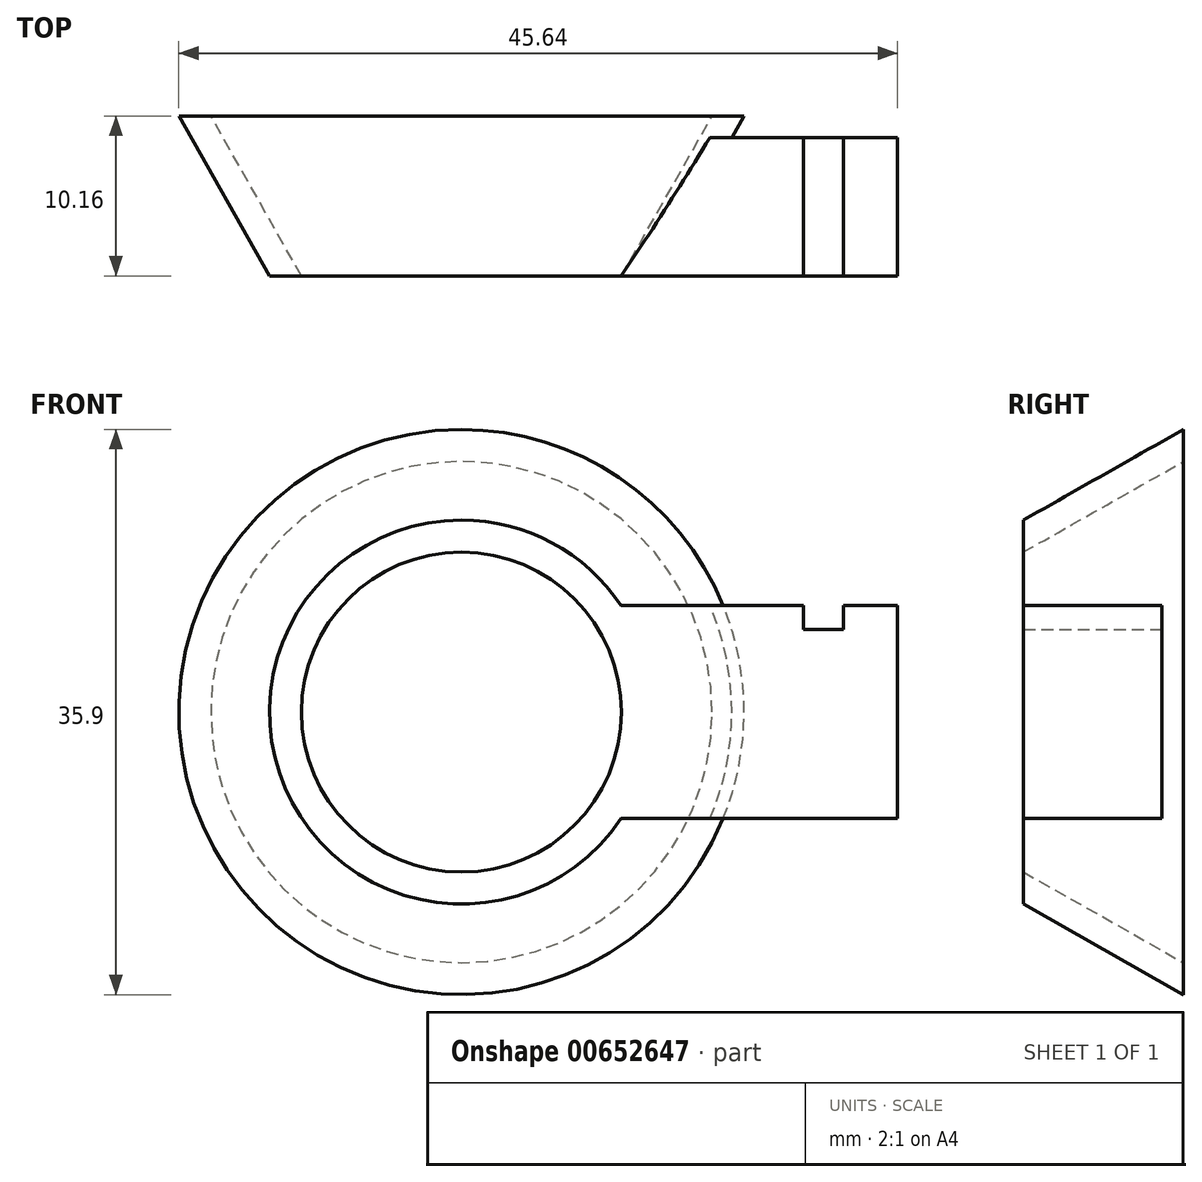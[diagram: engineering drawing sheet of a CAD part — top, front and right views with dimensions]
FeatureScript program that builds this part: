
annotation { "Feature Type Name" : "Feature", "Feature Type Description" : "" }
export const myFeature = defineFeature(function(context is Context, id is Id, definition is map)
    precondition{}
    {
        {
            var Q0;
            Q0=qCreatedBy(makeId("Top.planeOp"),FACE);
            var sketch = newSketch(context, id + "F0", { "sketchPlane" : qUnion([Q0])});
            skLineSegment(sketch, "E0.bottom", {"start": v(-10.16, -10.16) * mm, "end": v(10.16, -10.16) * mm, "construction": true});
            skLineSegment(sketch, "E0.top", {"start": v(-10.16, 10.16) * mm, "end": v(10.16, 10.16) * mm, "construction": true});
            skLineSegment(sketch, "E0.left", {"start": v(-10.16, -10.16) * mm, "end": v(-10.16, 10.16) * mm, "construction": true});
            skLineSegment(sketch, "E0.right", {"start": v(10.16, -10.16) * mm, "end": v(10.16, 10.16) * mm, "construction": true});
            skPoint(sketch, "E0.middle", {"position": v(0, 0) * mm});
            skLineSegment(sketch, "E1", {"start": v(-10.16, 0) * mm, "end": v(-15.92, 10.16) * mm});
            skLineSegment(sketch, "E2", {"start": v(-15.92, 10.16) * mm, "end": v(-17.95, 10.16) * mm});
            skLineSegment(sketch, "E3", {"start": v(-17.95, 10.16) * mm, "end": v(-12.2, 0) * mm});
            skLineSegment(sketch, "E4", {"start": v(-12.2, 0) * mm, "end": v(-10.16, 0) * mm});
            skLineSegment(sketch, "E5", {"start": v(0, 14.27) * mm, "end": v(0, -5.58) * mm});
            skSolve(sketch);
        }
        {
            var Q0;
            Q0=makeQuery(id+"F0.imprint","IMPRINT",FACE,{"disambiguationData":[TD([[makeQuery(id+"F0.imprint","IMPRINT",EDGE,{"derivedFrom":sQuery(id+"F0.wireOp",EDGE,"E1")}),1.0]])]});
            var Q1;
            Q1=sQuery(id+"F0.wireOp",EDGE,"E5");
            revolve(context, id + "F1", {"entities" : qUnion([Q0]), "axis" : qUnion([Q1]), "revolveType" : RevolveType.FULL});
        }
        {
            var Q0;
            Q0=qCreatedBy(makeId("Right.planeOp"),FACE);
            cPlane(context, id + "F2", {"entities" : qUnion([Q0]), "cplaneType" : CPlaneType.OFFSET, "offset" : 17.53 * mm, "width" : 152.4 * mm, "height" : 152.4 * mm});
        }
        {
            var Q0;
            Q0=qCreatedBy(id+"F2.planeOp",FACE);
            var sketch = newSketch(context, id + "F3", { "sketchPlane" : qUnion([Q0])});
            skLineSegment(sketch, "E6.bottom", {"start": v(0, 6.76) * mm, "end": v(8.79, 6.76) * mm});
            skLineSegment(sketch, "E6.top", {"start": v(0, -6.76) * mm, "end": v(8.79, -6.76) * mm});
            skLineSegment(sketch, "E6.left", {"start": v(0, 6.76) * mm, "end": v(0, -6.76) * mm});
            skLineSegment(sketch, "E6.right", {"start": v(8.79, 6.76) * mm, "end": v(8.79, -6.76) * mm});
            skPoint(sketch, "E6.middle", {"position": v(4.4, 0) * mm});
            skSolve(sketch);
        }
        {
            var Q0;
            Q0=makeQuery(id+"F3.imprint","IMPRINT",FACE,{"disambiguationData":[TD([[makeQuery(id+"F3.imprint","IMPRINT",EDGE,{"derivedFrom":sQuery(id+"F3.wireOp",EDGE,"E6.bottom")}),-1.0]])]});
            extrude(context, id + "F4", {"entities" : qUnion([Q0]), "operationType" : NewBodyOperationType.ADD, "endBound" : BoundingType.UP_TO_NEXT, "oppositeDirection" : true, "depth" : 25.4 * mm, "offsetDistance" : 25.4 * mm});
        }
        {
            var Q0;
            Q0=makeQuery(id+"F4.opExtrude","CAP_FACE",FACE,{"disambiguationData":[OSD([sQuery(id+"F3.wireOp",EDGE,"E6.bottom"),sQuery(id+"F3.wireOp",EDGE,"E6.top"),sQuery(id+"F3.wireOp",EDGE,"E6.left"),sQuery(id+"F3.wireOp",EDGE,"E6.right")])],"isStart":true});
            extrude(context, id + "F5", {"entities" : qUnion([Q0]), "operationType" : NewBodyOperationType.ADD, "depth" : 10.16 * mm, "offsetDistance" : 25.4 * mm});
        }
        {
            var Q0;
            {var subQ0=sQuery(id+"F3.wireOp",EDGE,"E6.bottom");Q0=makeQuery(id+"F5.boolean.opBoolean","MERGE",FACE,{"derivedFrom":[makeQuery(id+"F4.opExtrude","SWEPT_FACE",FACE,{"disambiguationData":[OSD([subQ0])]}),makeQuery(id+"F5.opExtrude","SWEPT_FACE",FACE,{"disambiguationData":[OSD([subQ0])]})]});}
            var sketch = newSketch(context, id + "F6", { "sketchPlane" : qUnion([Q0])});
            skLineSegment(sketch, "E7.bottom", {"start": v(24.27, 0) * mm, "end": v(21.73, 0) * mm});
            skLineSegment(sketch, "E7.top", {"start": v(24.27, 8.79) * mm, "end": v(21.73, 8.79) * mm});
            skLineSegment(sketch, "E7.left", {"start": v(24.27, 0) * mm, "end": v(24.27, 8.79) * mm});
            skLineSegment(sketch, "E7.right", {"start": v(21.73, 0) * mm, "end": v(21.73, 8.79) * mm});
            skSolve(sketch);
        }
        {
            var Q0;
            Q0=makeQuery(id+"F6.imprint","IMPRINT",FACE,{"disambiguationData":[TD([[makeQuery(id+"F6.imprint","IMPRINT",EDGE,{"derivedFrom":sQuery(id+"F6.wireOp",EDGE,"E7.bottom")}),1.0]])]});
            extrude(context, id + "F7", {"entities" : qUnion([Q0]), "operationType" : NewBodyOperationType.REMOVE, "oppositeDirection" : true, "depth" : 1.52 * mm, "offsetDistance" : 25.4 * mm});
        }
    });
